# Revit family: RPC Tree - Tropical
name_source: partatom
category: Planting
revit_build: Autodesk Revit Architecture 2012 (Build: 20110210_1515)
units: mm (PartAtom-declared; Revit-internal decimal feet)

## types (10) — shared parameters
Assembly Code = G2050500

## per-type parameters (varying)
| type | Height | Plan Symbol | Type Comments |
| Australian Tree Furn - 6' | 6' - 0" | Tropical Base | Australian Tree Furn |
| Buddha Belly Bamboo - 5' | 5' - 0" | Tropical Base | Buddha Belly Bamboo |
| Cuban Royal Palm - 25' | 25' - 0" | Tropical Base | Cuban Royal Palm |
| Golden Malay Palm - 10' | 10' - 0" | Tropical Base | Golden Malay Palm |
| Grass Palm - 18' | 18' - 0" | Tropical Base | Grass Palm |
| Hurricane Palm - 12' | 12' - 0" | Tropical Base | Hurricane Palm |
| Japanese Fiber Banana - 8' | 8' - 0" | Tropical Base | Japanese Fiber Banana |
| Orange Tree - 11' | 11' - 0" | Fruit Tree Base | Orange Tree |
| Travelers Palm - 13' | 13' - 0" | Tropical Base | Travelers Palm |
| Windmill Palm - 8' | 8' - 0" | Tropical Base | Windmill Palm |

## geometry (parser evidence)
native form markers: Sweep x2
no freeform markers — native parametric forms only
